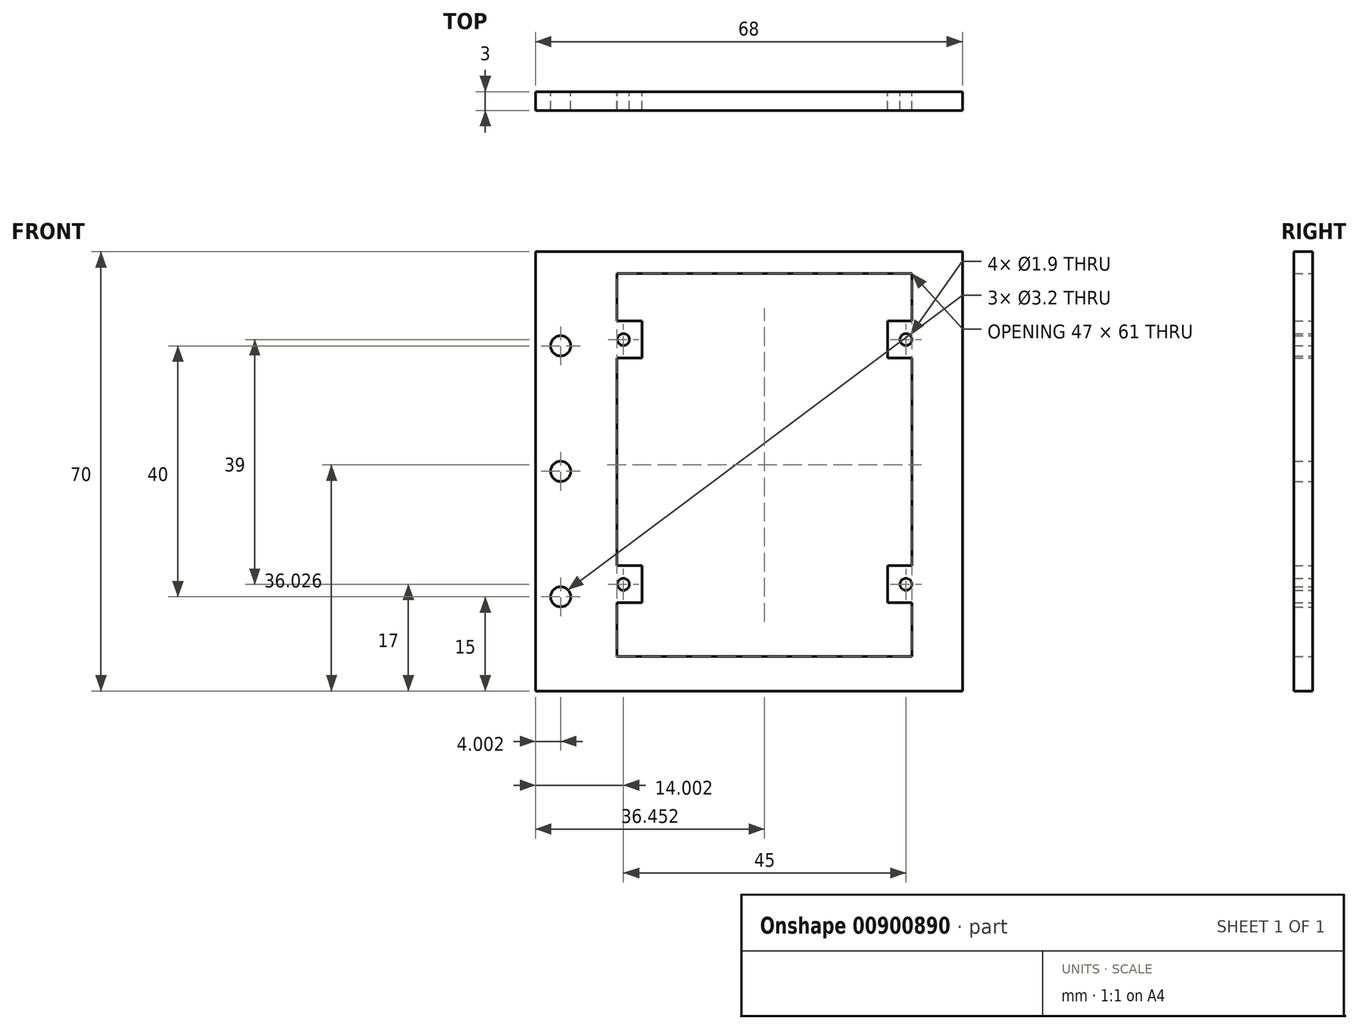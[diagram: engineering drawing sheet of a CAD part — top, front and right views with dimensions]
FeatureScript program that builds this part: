
annotation { "Feature Type Name" : "Feature", "Feature Type Description" : "" }
export const myFeature = defineFeature(function(context is Context, id is Id, definition is map)
    precondition{}
    {
        {
            var Q0;
            Q0=qCreatedBy(makeId("Front.planeOp"),FACE);
            var sketch = newSketch(context, id + "F0", { "sketchPlane" : qUnion([Q0])});
            skLineSegment(sketch, "E0.bottom", {"start": v(-30.47, 26.58) * mm, "end": v(37.53, 26.58) * mm});
            skLineSegment(sketch, "E0.top", {"start": v(-30.47, -43.42) * mm, "end": v(37.53, -43.42) * mm});
            skLineSegment(sketch, "E0.left", {"start": v(-30.47, 26.58) * mm, "end": v(-30.47, -43.42) * mm});
            skLineSegment(sketch, "E0.right", {"start": v(37.53, 26.58) * mm, "end": v(37.53, -43.42) * mm});
            skLineSegment(sketch, "E1", {"start": v(-16.47, 12.58) * mm, "end": v(28.53, 12.58) * mm, "construction": true});
            skLineSegment(sketch, "E2", {"start": v(28.53, 12.58) * mm, "end": v(28.53, -26.42) * mm, "construction": true});
            skLineSegment(sketch, "E3", {"start": v(28.53, -26.42) * mm, "end": v(-16.47, -26.42) * mm, "construction": true});
            skCircle(sketch, "E4", {"center": v(-16.47, 12.58) * mm, "radius": 0.95 * mm});
            skCircle(sketch, "E5", {"center": v(28.53, 12.58) * mm, "radius": 0.95 * mm});
            skCircle(sketch, "E6", {"center": v(28.53, -26.42) * mm, "radius": 0.95 * mm});
            skCircle(sketch, "E7", {"center": v(-16.47, -26.42) * mm, "radius": 0.95 * mm});
            skLineSegment(sketch, "E8", {"start": v(-16.47, 12.58) * mm, "end": v(-16.47, 26.58) * mm, "construction": true});
            skLineSegment(sketch, "E9", {"start": v(-16.47, -26.42) * mm, "end": v(-16.47, -43.42) * mm, "construction": true});
            skLineSegment(sketch, "E10", {"start": v(-30.47, 11.58) * mm, "end": v(-26.47, 11.58) * mm, "construction": true});
            skCircle(sketch, "E11", {"center": v(-26.47, 11.58) * mm, "radius": 1.6 * mm});
            skCircle(sketch, "E12", {"center": v(-26.47, -8.42) * mm, "radius": 1.6 * mm});
            skCircle(sketch, "E13", {"center": v(-26.47, -28.42) * mm, "radius": 1.6 * mm});
            skLineSegment(sketch, "E14", {"start": v(-26.47, 11.58) * mm, "end": v(-26.47, -8.42) * mm, "construction": true});
            skLineSegment(sketch, "E15", {"start": v(-26.47, -28.42) * mm, "end": v(-26.47, -8.42) * mm, "construction": true});
            skLineSegment(sketch, "E16", {"start": v(-26.47, 11.58) * mm, "end": v(-26.47, 26.58) * mm, "construction": true});
            skLineSegment(sketch, "E17.bottom", {"start": v(-17.52, 23.1) * mm, "end": v(29.48, 23.1) * mm});
            skLineSegment(sketch, "E17.top", {"start": v(-17.52, -37.9) * mm, "end": v(29.48, -37.9) * mm});
            skLineSegment(sketch, "E18.bottom", {"start": v(-17.52, 15.56) * mm, "end": v(-13.52, 15.56) * mm});
            skLineSegment(sketch, "E18.top", {"start": v(-17.52, 9.63) * mm, "end": v(-13.52, 9.63) * mm});
            skLineSegment(sketch, "E18.right", {"start": v(-13.52, 15.56) * mm, "end": v(-13.52, 9.63) * mm});
            skLineSegment(sketch, "E19.bottom", {"start": v(-17.52, -23.47) * mm, "end": v(-13.52, -23.47) * mm});
            skLineSegment(sketch, "E19.top", {"start": v(-17.52, -29.34) * mm, "end": v(-13.52, -29.34) * mm});
            skLineSegment(sketch, "E19.right", {"start": v(-13.52, -23.47) * mm, "end": v(-13.52, -29.34) * mm});
            skLineSegment(sketch, "E20.bottom", {"start": v(29.48, -29.37) * mm, "end": v(25.58, -29.37) * mm});
            skLineSegment(sketch, "E20.top", {"start": v(29.48, -23.47) * mm, "end": v(25.58, -23.47) * mm});
            skLineSegment(sketch, "E20.right", {"start": v(25.58, -29.37) * mm, "end": v(25.58, -23.47) * mm});
            skLineSegment(sketch, "E21.bottom", {"start": v(29.48, 15.53) * mm, "end": v(25.58, 15.53) * mm});
            skLineSegment(sketch, "E21.top", {"start": v(29.48, 9.63) * mm, "end": v(25.58, 9.63) * mm});
            skLineSegment(sketch, "E21.right", {"start": v(25.58, 15.53) * mm, "end": v(25.58, 9.63) * mm});
            skLineSegment(sketch, "E22", {"start": v(29.48, -29.37) * mm, "end": v(29.48, -37.9) * mm});
            skLineSegment(sketch, "E23", {"start": v(29.48, -23.47) * mm, "end": v(29.48, 9.63) * mm});
            skLineSegment(sketch, "E24", {"start": v(29.48, 15.53) * mm, "end": v(29.48, 23.1) * mm});
            skLineSegment(sketch, "E25", {"start": v(-17.52, -29.34) * mm, "end": v(-17.52, -37.9) * mm});
            skLineSegment(sketch, "E26", {"start": v(-17.52, -23.47) * mm, "end": v(-17.52, 9.63) * mm});
            skLineSegment(sketch, "E27", {"start": v(-17.52, 23.1) * mm, "end": v(-17.52, 15.56) * mm});
            skSolve(sketch);
        }
        {
            var Q0;
            Q0 = qSketchRegion(id + "F0", true);
            var Q1;
            Q1=makeQuery(id+"F0.imprint","IMPRINT",FACE,{"disambiguationData":[TD([[makeQuery(id+"F0.imprint","IMPRINT",EDGE,{"derivedFrom":sQuery(id+"F0.wireOp",EDGE,"E4")}),-1.0]])]});
            var Q2;
            {var subQ3=sQuery(id+"F0.wireOp",EDGE,"E5");Q2=makeQuery(id+"F0.imprint","IMPRINT",FACE,{"disambiguationData":[TD([[makeQuery(id+"F0.imprint","IMPRINT",EDGE,{"derivedFrom":subQ3}),-1.0]])]});}
            var Q3;
            Q3=makeQuery(id+"F0.imprint","IMPRINT",FACE,{"disambiguationData":[TD([[makeQuery(id+"F0.imprint","IMPRINT",EDGE,{"derivedFrom":sQuery(id+"F0.wireOp",EDGE,"E7")}),-1.0]])]});
            var Q4;
            {var subQ3=sQuery(id+"F0.wireOp",EDGE,"E6");Q4=makeQuery(id+"F0.imprint","IMPRINT",FACE,{"disambiguationData":[TD([[makeQuery(id+"F0.imprint","IMPRINT",EDGE,{"derivedFrom":subQ3}),-1.0]])]});}
            extrude(context, id + "F1", {"entities" : qUnion([Q0, Q1, Q2, Q3, Q4]), "depth" : 3 * mm, "offsetDistance" : 25 * mm});
        }
    });
